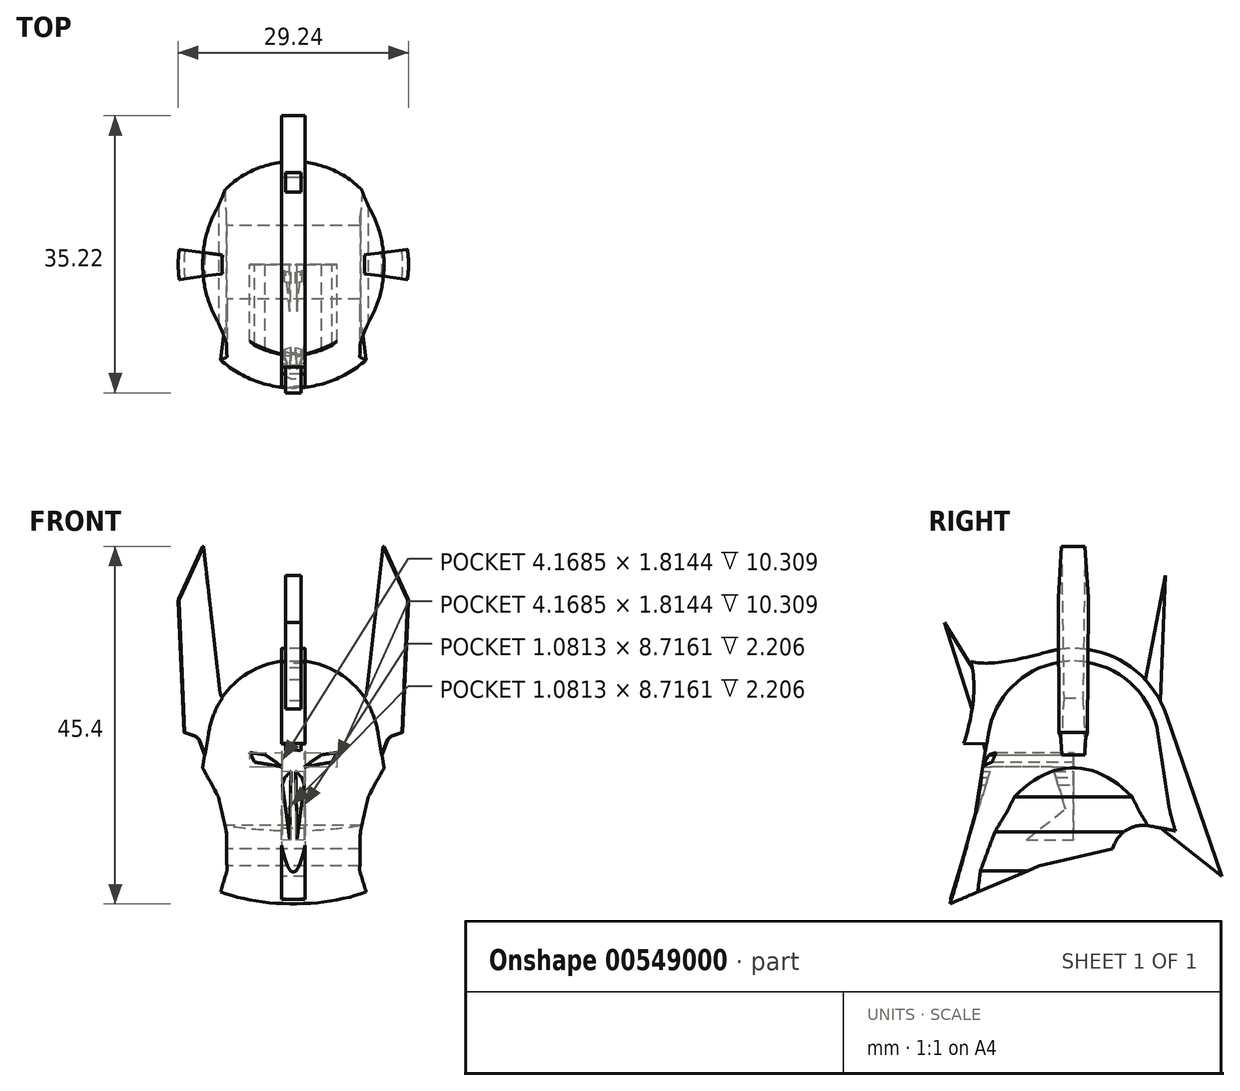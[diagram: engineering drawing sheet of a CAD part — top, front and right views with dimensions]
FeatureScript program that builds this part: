
annotation { "Feature Type Name" : "Feature", "Feature Type Description" : "" }
export const myFeature = defineFeature(function(context is Context, id is Id, definition is map)
    precondition{}
    {
        {
            var Q0;
            Q0=qCreatedBy(makeId("Front.planeOp"),FACE);
            var sketch = newSketch(context, id + "F0", { "sketchPlane" : qUnion([Q0])});
            skArc(sketch, "E0", {"start": v(10.88, 1.65) * mm, "mid": v(0, 11) * mm, "end": v(-10.88, 1.65) * mm});
            skArc(sketch, "E1", {"start": v(-5.37, -21.29) * mm, "mid": v(7.45, -20.04) * mm, "end": v(12.36, -8.12) * mm});
            skLineSegment(sketch, "E2", {"start": v(-10.88, 1.65) * mm, "end": v(-12.33, -7.95) * mm});
            skLineSegment(sketch, "E3", {"start": v(12.36, -8.12) * mm, "end": v(10.88, 1.65) * mm});
            skLineSegment(sketch, "E4", {"start": v(0, 11) * mm, "end": v(0, -22.5) * mm});
            skLineSegment(sketch, "E5", {"start": v(-12.5, -8.69) * mm, "end": v(-15.76, -20.2) * mm});
            skLineSegment(sketch, "E6", {"start": v(-15.76, -20.2) * mm, "end": v(-5.37, -21.29) * mm});
            skPoint(sketch, "E7.visualSharp", {"position": v(-12.39, -8.33) * mm});
            skArc(sketch, "E7.filletArc", {"start": v(-12.5, -8.69) * mm, "mid": v(-12.4, -8.32) * mm, "end": v(-12.33, -7.95) * mm});
            skSolve(sketch);
        }
        {
            var Q0;
            {var subQ0=sQuery(id+"F0.wireOp",EDGE,"E2");Q0=makeQuery(id+"F0.imprint","IMPRINT",FACE,{"disambiguationData":[TD([[makeQuery(id+"F0.imprint","IMPRINT",EDGE,{"derivedFrom":subQ0}),1.0]])]});}
            var Q1;
            Q1=sQuery(id+"F0.wireOp",EDGE,"E4");
            revolve(context, id + "F1", {"entities" : qUnion([Q0]), "axis" : qUnion([Q1]), "revolveType" : RevolveType.FULL});
        }
        {
            var Q0;
            Q0=qCreatedBy(makeId("Right.planeOp"),FACE);
            var sketch = newSketch(context, id + "F2", { "sketchPlane" : qUnion([Q0])});
            skFitSpline(sketch, "E8", {"points": [v(-15.56, -2.93) * mm, v(-13.03, 10.85) * mm], "startDerivative": vector(4.8, 5.87) * mm, "endDerivative": vector(-4.04, 13.5) * mm});
            skArc(sketch, "E9", {"start": v(11.82, 4.07) * mm, "mid": v(5.84, 11.05) * mm, "end": v(-3.3, 12.06) * mm});
            skFitSpline(sketch, "E10", {"points": [v(-3.3, 12.06) * mm, v(-13.03, 10.85) * mm], "startDerivative": vector(-12.76, -3.5) * mm, "endDerivative": vector(-6.8, 1.76) * mm});
            skLineSegment(sketch, "E11", {"start": v(11.82, 4.07) * mm, "end": v(18.89, -16.44) * mm});
            skLineSegment(sketch, "E12", {"start": v(18.89, -16.44) * mm, "end": v(4.3, -4.97) * mm});
            skLineSegment(sketch, "E13", {"start": v(4.3, -4.97) * mm, "end": v(1.77, -3.53) * mm});
            skLineSegment(sketch, "E14", {"start": v(1.77, -3.53) * mm, "end": v(1.35, -1.31) * mm});
            skLineSegment(sketch, "E15", {"start": v(1.35, -1.31) * mm, "end": v(0, 0) * mm});
            skLineSegment(sketch, "E16", {"start": v(0, 0) * mm, "end": v(-3.13, -0.88) * mm});
            skLineSegment(sketch, "E17", {"start": v(-3.13, -0.88) * mm, "end": v(-0.99, -7.89) * mm});
            skLineSegment(sketch, "E18", {"start": v(-0.99, -7.89) * mm, "end": v(-15.61, -19.4) * mm});
            skLineSegment(sketch, "E19", {"start": v(-15.61, -19.4) * mm, "end": v(-9.52, 0.39) * mm});
            skLineSegment(sketch, "E20", {"start": v(-9.52, 0.39) * mm, "end": v(-13.93, 0.42) * mm});
            skSolve(sketch);
        }
        {
            var Q0;
            Q0=qCreatedBy(makeId("Front.planeOp"),FACE);
            var sketch = newSketch(context, id + "F3", { "sketchPlane" : qUnion([Q0])});
            skLineSegment(sketch, "E21", {"start": v(-0.3, -3.1) * mm, "end": v(-1.1, -3.9) * mm});
            skLineSegment(sketch, "E22", {"start": v(-1.1, -3.9) * mm, "end": v(-1.38, -4.83) * mm});
            skLineSegment(sketch, "E23", {"start": v(-1.38, -4.83) * mm, "end": v(-0.45, -11.8) * mm});
            skLineSegment(sketch, "E24", {"start": v(-0.45, -11.8) * mm, "end": v(-0.3, -3.1) * mm});
            skLineSegment(sketch, "E25", {"start": v(1.36, -2.55) * mm, "end": v(4.91, -1.93) * mm});
            skLineSegment(sketch, "E26", {"start": v(4.91, -1.93) * mm, "end": v(5.53, -0.74) * mm});
            skLineSegment(sketch, "E27", {"start": v(5.53, -0.74) * mm, "end": v(3.57, -1) * mm});
            skLineSegment(sketch, "E28", {"start": v(3.57, -1) * mm, "end": v(1.36, -2.55) * mm});
            skLineSegment(sketch, "E29.MirrorCS", {"start": v(0.3, -3.1) * mm, "end": v(1.1, -3.9) * mm});
            skLineSegment(sketch, "E30.MirrorCS", {"start": v(0.45, -11.8) * mm, "end": v(0.3, -3.1) * mm});
            skLineSegment(sketch, "E31.MirrorCS", {"start": v(1.38, -4.83) * mm, "end": v(0.45, -11.8) * mm});
            skLineSegment(sketch, "E32.MirrorCS", {"start": v(1.1, -3.9) * mm, "end": v(1.38, -4.83) * mm});
            skLineSegment(sketch, "E33.MirrorCS", {"start": v(-5.53, -0.74) * mm, "end": v(-3.57, -1) * mm});
            skLineSegment(sketch, "E34.MirrorCS", {"start": v(-4.91, -1.93) * mm, "end": v(-5.53, -0.74) * mm});
            skLineSegment(sketch, "E35.MirrorCS", {"start": v(-3.57, -1) * mm, "end": v(-1.36, -2.55) * mm});
            skLineSegment(sketch, "E36.MirrorCS", {"start": v(-1.36, -2.55) * mm, "end": v(-4.91, -1.93) * mm});
            skLineSegment(sketch, "E37", {"start": v(-13.9, 1.85) * mm, "end": v(-14.62, 18.48) * mm});
            skLineSegment(sketch, "E38", {"start": v(-14.53, 18.94) * mm, "end": v(-11.52, 25.46) * mm});
            skLineSegment(sketch, "E39", {"start": v(-11.52, 25.46) * mm, "end": v(-9.37, 6.82) * mm});
            skLineSegment(sketch, "E40", {"start": v(-8.37, 5.93) * mm, "end": v(8.37, 5.93) * mm});
            skLineSegment(sketch, "E41", {"start": v(9.37, 6.82) * mm, "end": v(11.52, 25.46) * mm});
            skLineSegment(sketch, "E42", {"start": v(11.52, 25.46) * mm, "end": v(14.53, 18.94) * mm});
            skLineSegment(sketch, "E43", {"start": v(14.62, 18.48) * mm, "end": v(13.9, 1.85) * mm});
            skLineSegment(sketch, "E44", {"start": v(-10.76, -2.3) * mm, "end": v(-7.74, 0) * mm});
            skLineSegment(sketch, "E45", {"start": v(-7.74, 0) * mm, "end": v(7.74, 0) * mm});
            skLineSegment(sketch, "E46", {"start": v(7.74, 0) * mm, "end": v(10.76, -2.3) * mm});
            skLineSegment(sketch, "E47", {"start": v(-13.9, 1.85) * mm, "end": v(-12.57, 1.36) * mm});
            skLineSegment(sketch, "E48", {"start": v(-11.99, 0.8) * mm, "end": v(-10.76, -2.3) * mm});
            skLineSegment(sketch, "E49", {"start": v(10.76, -2.3) * mm, "end": v(11.99, 0.8) * mm});
            skLineSegment(sketch, "E50", {"start": v(12.57, 1.36) * mm, "end": v(13.9, 1.85) * mm});
            skPoint(sketch, "E51.visualSharp", {"position": v(-9.26, 5.93) * mm});
            skArc(sketch, "E51.filletArc", {"start": v(-9.37, 6.82) * mm, "mid": v(-9.04, 6.18) * mm, "end": v(-8.37, 5.93) * mm});
            skPoint(sketch, "E52.visualSharp", {"position": v(9.26, 5.93) * mm});
            skArc(sketch, "E52.filletArc", {"start": v(8.37, 5.93) * mm, "mid": v(9.04, 6.18) * mm, "end": v(9.37, 6.82) * mm});
            skPoint(sketch, "E53.visualSharp", {"position": v(12.15, 1.2) * mm});
            skArc(sketch, "E53.filletArc", {"start": v(12.57, 1.36) * mm, "mid": v(12.22, 1.14) * mm, "end": v(11.99, 0.8) * mm});
            skPoint(sketch, "E54.visualSharp", {"position": v(-12.15, 1.2) * mm});
            skArc(sketch, "E54.filletArc", {"start": v(-11.99, 0.8) * mm, "mid": v(-12.22, 1.14) * mm, "end": v(-12.57, 1.36) * mm});
            skPoint(sketch, "E55.visualSharp", {"position": v(-14.63, 18.72) * mm});
            skArc(sketch, "E55.filletArc", {"start": v(-14.53, 18.94) * mm, "mid": v(-14.6, 18.71) * mm, "end": v(-14.62, 18.48) * mm});
            skPoint(sketch, "E56.visualSharp", {"position": v(14.63, 18.72) * mm});
            skArc(sketch, "E56.filletArc", {"start": v(14.62, 18.48) * mm, "mid": v(14.6, 18.71) * mm, "end": v(14.53, 18.94) * mm});
            skLineSegment(sketch, "E57", {"start": v(0, 5.93) * mm, "end": v(0, 0) * mm});
            skSolve(sketch);
        }
        {
            var Q0;
            Q0=makeQuery(id+"F3.imprint","IMPRINT",FACE,{"disambiguationData":[TD([[makeQuery(id+"F3.imprint","IMPRINT",EDGE,{"derivedFrom":sQuery(id+"F3.wireOp",EDGE,"E37")}),-1.0]])]});
            var Q1;
            Q1=sQuery(id+"F0.wireOp",EDGE,"E4");
            revolve(context, id + "F4", {"operationType" : NewBodyOperationType.ADD, "entities" : qUnion([Q0]), "axis" : qUnion([Q1]), "revolveType" : RevolveType.SYMMETRIC, "oppositeDirection" : true, "angle" : 15 * degree});
        }
        {
            var Q0;
            Q0=makeQuery(id+"F3.imprint","IMPRINT",FACE,{"disambiguationData":[TD([[makeQuery(id+"F3.imprint","IMPRINT",EDGE,{"derivedFrom":sQuery(id+"F3.wireOp",EDGE,"E41")}),-1.0]])]});
            var Q1;
            Q1=sQuery(id+"F3.wireOp",EDGE,"E57");
            revolve(context, id + "F5", {"operationType" : NewBodyOperationType.ADD, "entities" : qUnion([Q0]), "axis" : qUnion([Q1]), "revolveType" : RevolveType.SYMMETRIC, "angle" : 15 * degree});
        }
        {
            var Q0;
            Q0=makeQuery(id+"F3.imprint","IMPRINT",FACE,{"disambiguationData":[TD([[makeQuery(id+"F3.imprint","IMPRINT",EDGE,{"derivedFrom":sQuery(id+"F3.wireOp",EDGE,"E33.MirrorCS")}),-1.0]])]});
            var Q1;
            Q1=makeQuery(id+"F3.imprint","IMPRINT",FACE,{"disambiguationData":[TD([[makeQuery(id+"F3.imprint","IMPRINT",EDGE,{"derivedFrom":sQuery(id+"F3.wireOp",EDGE,"E25")}),1.0]])]});
            var Q2;
            Q2=makeQuery(id+"F3.imprint","IMPRINT",FACE,{"disambiguationData":[TD([[makeQuery(id+"F3.imprint","IMPRINT",EDGE,{"derivedFrom":sQuery(id+"F3.wireOp",EDGE,"E29.MirrorCS")}),-1.0]])]});
            var Q3;
            Q3=makeQuery(id+"F3.imprint","IMPRINT",FACE,{"disambiguationData":[TD([[makeQuery(id+"F3.imprint","IMPRINT",EDGE,{"derivedFrom":sQuery(id+"F3.wireOp",EDGE,"E21")}),1.0]])]});
            extrude(context, id + "F6", {"entities" : qUnion([Q0, Q1, Q2, Q3]), "operationType" : NewBodyOperationType.REMOVE, "depth" : 25 * mm, "offsetDistance" : 25 * mm});
        }
        {
            var Q0;
            Q0=qCreatedBy(makeId("Right.planeOp"),FACE);
            var sketch = newSketch(context, id + "F7", { "sketchPlane" : qUnion([Q0])});
            skLineSegment(sketch, "E58", {"start": v(10.82, 0) * mm, "end": v(11.68, 21.77) * mm});
            skLineSegment(sketch, "E59", {"start": v(11.68, 21.77) * mm, "end": v(8.19, 3.4) * mm});
            skLineSegment(sketch, "E60", {"start": v(8.19, 3.4) * mm, "end": v(-8.78, 3.4) * mm});
            skLineSegment(sketch, "E61", {"start": v(-8.78, 3.4) * mm, "end": v(-16.33, 15.82) * mm});
            skLineSegment(sketch, "E62", {"start": v(-16.33, 15.82) * mm, "end": v(-10.44, -2.75) * mm});
            skLineSegment(sketch, "E63", {"start": v(-10.44, -2.75) * mm, "end": v(10.82, 0) * mm});
            skSolve(sketch);
        }
        {
            var Q0;
            Q0 = qSketchRegion(id + "F7", true);
            extrude(context, id + "F8", {"entities" : qUnion([Q0]), "operationType" : NewBodyOperationType.ADD, "endBound" : BoundingType.SYMMETRIC, "depth" : 2 * mm, "offsetDistance" : 25 * mm});
        }
        {
            var Q0;
            Q0=qCreatedBy(makeId("Right.planeOp"),FACE);
            var sketch = newSketch(context, id + "F9", { "sketchPlane" : qUnion([Q0])});
            skLineSegment(sketch, "E64", {"start": v(-4.38, -15.15) * mm, "end": v(4.96, -12.96) * mm});
            skLineSegment(sketch, "E65", {"start": v(4.96, -12.96) * mm, "end": v(5.25, -12.31) * mm});
            skLineSegment(sketch, "E66", {"start": v(9.67, -10.03) * mm, "end": v(18.41, -11.75) * mm});
            skLineSegment(sketch, "E67", {"start": v(18.41, -11.75) * mm, "end": v(20.17, -21.15) * mm});
            skLineSegment(sketch, "E68", {"start": v(20.17, -21.15) * mm, "end": v(-21.1, -26.85) * mm});
            skLineSegment(sketch, "E69", {"start": v(-21.1, -26.85) * mm, "end": v(-17.71, -20.8) * mm});
            skLineSegment(sketch, "E70", {"start": v(-17.71, -20.8) * mm, "end": v(-4.38, -15.15) * mm});
            skPoint(sketch, "E71.visualSharp", {"position": v(6.56, -9.42) * mm});
            skArc(sketch, "E71.filletArc", {"start": v(9.67, -10.03) * mm, "mid": v(7.06, -10.4) * mm, "end": v(5.25, -12.31) * mm});
            skSolve(sketch);
        }
        {
            var Q0;
            Q0 = qSketchRegion(id + "F9", true);
            extrude(context, id + "F10", {"entities" : qUnion([Q0]), "operationType" : NewBodyOperationType.REMOVE, "endBound" : BoundingType.SYMMETRIC, "depth" : 55 * mm, "offsetDistance" : 25 * mm});
        }
        {
            var Q0;
            Q0=qCreatedBy(makeId("Front.planeOp"),FACE);
            var sketch = newSketch(context, id + "F11", { "sketchPlane" : qUnion([Q0])});
            skLineSegment(sketch, "E72", {"start": v(0, 0) * mm, "end": v(0, -14.9) * mm, "construction": true});
            skLineSegment(sketch, "E73", {"start": v(-9.33, -18.74) * mm, "end": v(-14.77, -18.78) * mm});
            skLineSegment(sketch, "E74", {"start": v(-14.77, -18.78) * mm, "end": v(-19.48, -15.8) * mm});
            skLineSegment(sketch, "E75", {"start": v(-19.48, -15.8) * mm, "end": v(-18.97, -7.3) * mm});
            skLineSegment(sketch, "E76", {"start": v(-18.97, -7.3) * mm, "end": v(-19.72, -2.66) * mm});
            skLineSegment(sketch, "E77", {"start": v(-19.72, -2.66) * mm, "end": v(-19.08, 1.45) * mm});
            skLineSegment(sketch, "E78", {"start": v(-19.08, 1.45) * mm, "end": v(-13.27, 0.56) * mm});
            skLineSegment(sketch, "E79", {"start": v(-13.27, 0.56) * mm, "end": v(-9.5, -6.39) * mm});
            skLineSegment(sketch, "E80", {"start": v(-8.51, -10.78) * mm, "end": v(-9.5, -6.39) * mm});
            skLineSegment(sketch, "E81", {"start": v(-8.51, -10.78) * mm, "end": v(-8.43, -15.73) * mm});
            skLineSegment(sketch, "E82", {"start": v(-8.43, -15.73) * mm, "end": v(-9.33, -18.74) * mm});
            skLineSegment(sketch, "E83.MirrorCS", {"start": v(8.43, -15.73) * mm, "end": v(9.33, -18.74) * mm});
            skLineSegment(sketch, "E84.MirrorCS", {"start": v(8.51, -10.78) * mm, "end": v(9.5, -6.39) * mm});
            skLineSegment(sketch, "E85.MirrorCS", {"start": v(19.48, -15.8) * mm, "end": v(18.97, -7.3) * mm});
            skLineSegment(sketch, "E86.MirrorCS", {"start": v(13.27, 0.56) * mm, "end": v(9.5, -6.39) * mm});
            skLineSegment(sketch, "E87.MirrorCS", {"start": v(8.51, -10.78) * mm, "end": v(8.43, -15.73) * mm});
            skLineSegment(sketch, "E88.MirrorCS", {"start": v(9.33, -18.74) * mm, "end": v(14.77, -18.78) * mm});
            skLineSegment(sketch, "E89.MirrorCS", {"start": v(14.77, -18.78) * mm, "end": v(19.48, -15.8) * mm});
            skLineSegment(sketch, "E90.MirrorCS", {"start": v(18.97, -7.3) * mm, "end": v(19.72, -2.66) * mm});
            skLineSegment(sketch, "E91.MirrorCS", {"start": v(19.72, -2.66) * mm, "end": v(19.08, 1.45) * mm});
            skLineSegment(sketch, "E92.MirrorCS", {"start": v(19.08, 1.45) * mm, "end": v(13.27, 0.56) * mm});
            skSolve(sketch);
        }
        {
            var Q0;
            Q0 = qSketchRegion(id + "F11", true);
            extrude(context, id + "F12", {"entities" : qUnion([Q0]), "operationType" : NewBodyOperationType.REMOVE, "endBound" : BoundingType.SYMMETRIC, "oppositeDirection" : true, "depth" : 555 * mm, "offsetDistance" : 25 * mm});
        }
        {
            var Q0;
            Q0 = qSketchRegion(id + "F2", true);
            extrude(context, id + "F13", {"entities" : qUnion([Q0]), "operationType" : NewBodyOperationType.ADD, "endBound" : BoundingType.SYMMETRIC, "depth" : 3 * mm, "offsetDistance" : 25 * mm});
        }
    });
